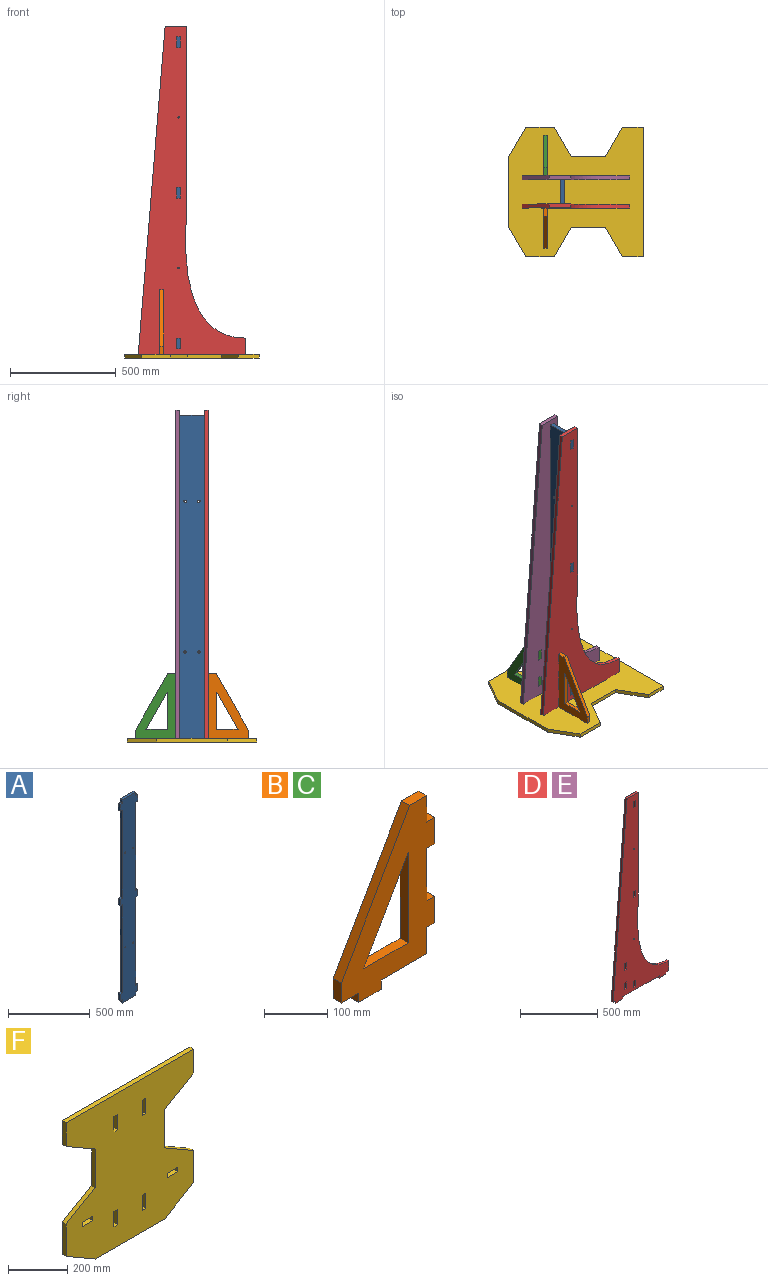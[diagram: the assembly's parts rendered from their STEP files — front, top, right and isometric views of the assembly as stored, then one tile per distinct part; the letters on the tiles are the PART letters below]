
ASSEMBLY  parts=6 mates=5
PART A: 34 faces, bbox 152.4x18x1524 mm
  f0: plane 25.4x18.03mm, normal (1,0,0), area 458.1mm2, adj f1,f30,f32,f33
  f1: plane 18.03x18.03mm, normal (0,0,-1), area 325.2mm2, adj f0,f2,f32,f33
  f2: plane 50.8x18.03mm, normal (1,0,0), area 916.1mm2, adj f1,f3,f32,f33
  f3: plane 18.03x18.03mm, normal (0,0,1), area 325.2mm2, adj f2,f4,f32,f33
  f4: plane 660.4x18.03mm, normal (1,0,0), area 11909.7mm2, adj f3,f5,f32,f33
  f5: plane 18.03x18.03mm, normal (0,0,-1), area 325.2mm2, adj f4,f6,f32,f33
  f6: plane 50.8x18.03mm, normal (1,0,0), area 916.1mm2, adj f5,f7,f32,f33
  f7: plane 18.03x18.03mm, normal (0,0,1), area 325.2mm2, adj f6,f8,f32,f33
  f8: plane 660.4x18.03mm, normal (1,0,0), area 11909.7mm2, adj f7,f9,f32,f33
  f9: plane 18.03x18.03mm, normal (0,0,-1), area 325.2mm2, adj f8,f10,f32,f33
  f10: plane 50.8x18.03mm, normal (1,0,0), area 916.1mm2, adj f9,f11,f32,f33
  f11: plane 18.03x18.03mm, normal (0,0,1), area 325.2mm2, adj f10,f12,f32,f33
  f12: plane 25.4x18.03mm, normal (1,0,0), area 458.1mm2, adj f11,f13,f32,f33
  f13: plane 116.33x18.03mm, normal (0,0,1), area 2097.9mm2, adj f12,f14,f32,f33
  f14: plane 25.4x18.03mm, normal (-1,0,0), area 458.1mm2, adj f13,f15,f32,f33
  f15: plane 18.03x18.03mm, normal (0,0,1), area 325.2mm2, adj f14,f16,f32,f33
  f16: plane 50.8x18.03mm, normal (-1,0,0), area 916.1mm2, adj f15,f17,f32,f33
  f17: plane 18.03x18.03mm, normal (0,0,-1), area 325.2mm2, adj f16,f18,f32,f33
  f18: plane 660.4x18.03mm, normal (-1,0,0), area 11909.7mm2, adj f17,f19,f32,f33
  f19: plane 18.03x18.03mm, normal (0,0,1), area 325.2mm2, adj f18,f20,f32,f33
  f20: plane 50.8x18.03mm, normal (-1,0,0), area 916.1mm2, adj f19,f21,f32,f33
  f21: plane 18.03x18.03mm, normal (0,0,-1), area 325.2mm2, adj f20,f22,f32,f33
  f22: plane 660.4x18.03mm, normal (-1,0,0), area 11909.7mm2, adj f21,f23,f32,f33
  f23: plane 18.03x18.03mm, normal (0,0,1), area 325.2mm2, adj f22,f24,f32,f33
  f24: plane 50.8x18.03mm, normal (-1,0,0), area 916.1mm2, adj f23,f25,f32,f33
  f25: plane 18.03x18.03mm, normal (0,0,-1), area 325.2mm2, adj f24,f26,f32,f33
  f26: plane 25.4x18.03mm, normal (-1,0,0), area 458.1mm2, adj f25,f30,f32,f33
  f27: cylinder r=5.59mm len=18.03mm, axis (0,1,0), area 633.2mm2, adj f32,f33
  f28: cylinder r=5.59mm len=18.03mm, axis (0,1,0), area 633.2mm2, adj f32,f33
  f29: cylinder r=5.59mm len=18.03mm, axis (0,1,0), area 633.2mm2, adj f32,f33
  f30: plane 116.33x18.03mm, normal (0,0,-1), area 2097.9mm2, adj f0,f26,f32,f33
  f31: cylinder r=5.59mm len=18.03mm, axis (0,1,0), area 633.2mm2, adj f32,f33
  f32: plane 1524x152.4mm, normal (0,-1,0), area 182394.3mm2, adj f0,f1,f2,f3,f4,f5,f6,f7
  f33: plane 1524x152.4mm, normal (0,1,0), area 182394.3mm2, adj f0,f1,f2,f3,f4,f5,f6,f7
PART B: 22 faces, bbox 208.5x18x322.8 mm
  f0: plane 50.8x18.03mm, normal (1,0,0), area 916.1mm2, adj f1,f19,f20,f21
  f1: plane 18.03x18.03mm, normal (0,0,-1), area 325.2mm2, adj f0,f2,f20,f21
  f2: plane 50.8x18.03mm, normal (1,0,0), area 916.1mm2, adj f1,f3,f20,f21
  f3: plane 18.03x18.03mm, normal (0,0,1), area 325.2mm2, adj f2,f4,f20,f21
  f4: plane 101.6x18.03mm, normal (1,0,0), area 1832.3mm2, adj f3,f5,f20,f21
  f5: plane 18.03x18.03mm, normal (0,0,-1), area 325.2mm2, adj f4,f6,f20,f21
  f6: plane 50.8x18.03mm, normal (1,0,0), area 916.1mm2, adj f5,f7,f20,f21
  f7: plane 18.03x18.03mm, normal (0,0,1), area 325.2mm2, adj f6,f8,f20,f21
  f8: plane 50.8x18.03mm, normal (1,0,0), area 916.1mm2, adj f7,f9,f20,f21
  f9: plane 38.1x18.03mm, normal (0,0,1), area 687.1mm2, adj f8,f10,f20,f21
  f10: plane 266.7x152.4mm, normal (-0.87,0,0.5), area 5539.5mm2, adj f9,f11,f20,f21
  f11: plane 38.1x18.03mm, normal (-1,0,0), area 687.1mm2, adj f10,f12,f20,f21
  f12: plane 38.1x18.03mm, normal (0,0,-1), area 687.1mm2, adj f11,f13,f20,f21
  f13: plane 18.03x18.03mm, normal (-1,0,0), area 325.2mm2, adj f12,f14,f20,f21
  f14: plane 50.8x18.03mm, normal (0,0,-1), area 916.1mm2, adj f13,f15,f20,f21
  f15: plane 18.03x18.03mm, normal (1,0,0), area 325.2mm2, adj f14,f19,f20,f21
  f16: plane 174.78x18.03mm, normal (-1,0,0), area 3151.9mm2, adj f17,f18,f20,f21
  f17: plane 99.87x18.03mm, normal (0,0,1), area 1801.1mm2, adj f16,f18,f20,f21
  f18: plane 174.78x99.87mm, normal (0.87,0,-0.5), area 3630.2mm2, adj f16,f17,f20,f21
  f19: plane 101.6x18.03mm, normal (0,0,-1), area 1832.3mm2, adj f0,f15,f20,f21
  f20: plane 322.83x208.53mm, normal (0,-1,0), area 31762.6mm2, adj f0,f1,f2,f3,f4,f5,f6,f7
  f21: plane 322.83x208.53mm, normal (0,1,0), area 31762.6mm2, adj f0,f1,f2,f3,f4,f5,f6,f7
PART C: same geometry as B
PART D: 38 faces, bbox 508x18x1567.4 mm
  f0: plane 25.4x18.03mm, normal (0,0,-1), area 458.1mm2, adj f1,f35,f36,f37
  f1: plane 18.03x18.03mm, normal (-1,0,0), area 325.2mm2, adj f0,f2,f36,f37
  f2: plane 63.5x18.03mm, normal (0,0,-1), area 1145.2mm2, adj f1,f3,f36,f37
  f3: plane 18.03x18.03mm, normal (1,0,0), area 325.2mm2, adj f2,f4,f36,f37
  f4: plane 330.2x18.03mm, normal (0,0,-1), area 5954.8mm2, adj f3,f5,f36,f37
  f5: plane 18.03x18.03mm, normal (-1,0,0), area 325.2mm2, adj f4,f6,f36,f37
  f6: plane 63.5x18.03mm, normal (0,0,-1), area 1145.2mm2, adj f5,f7,f36,f37
  f7: plane 18.03x18.03mm, normal (1,0,0), area 325.2mm2, adj f6,f8,f36,f37
  f8: plane 25.4x18.03mm, normal (0,0,-1), area 458.1mm2, adj f7,f9,f36,f37
  f9: plane 76.2x18.03mm, normal (1,0,0), area 1374.2mm2, adj f8,f10,f36,f37
  f10: extruded ~635x286.15mm, area 14161.2mm2, adj f9,f11,f36,f37
  f11: plane 838.2x18.03mm, normal (1,0,0), area 15116.1mm2, adj f10,f12,f36,f37
  f12: plane 101.6x18.03mm, normal (0,0,1), area 1832.3mm2, adj f11,f35,f36,f37
  f13: plane 50.8x18.03mm, normal (-1,0,0), area 916.1mm2, adj f14,f30,f36,f37
  f14: plane 18.03x18.03mm, normal (0,0,1), area 325.2mm2, adj f13,f15,f36,f37
  f15: plane 50.8x18.03mm, normal (1,0,0), area 916.1mm2, adj f14,f30,f36,f37
  f16: plane 50.8x18.03mm, normal (1,0,0), area 916.1mm2, adj f17,f31,f36,f37
  f17: plane 18.03x18.03mm, normal (0,0,-1), area 325.2mm2, adj f16,f18,f36,f37
  f18: plane 50.8x18.03mm, normal (-1,0,0), area 916.1mm2, adj f17,f31,f36,f37
  f19: plane 50.8x18.03mm, normal (1,0,0), area 916.1mm2, adj f20,f32,f36,f37
  f20: plane 18.03x18.03mm, normal (0,0,-1), area 325.2mm2, adj f19,f21,f36,f37
  f21: plane 50.8x18.03mm, normal (-1,0,0), area 916.1mm2, adj f20,f32,f36,f37
  f22: plane 18.03x18.03mm, normal (0,0,1), area 325.2mm2, adj f23,f33,f36,f37
  f23: plane 50.8x18.03mm, normal (1,0,0), area 916.1mm2, adj f22,f24,f36,f37
  f24: plane 18.03x18.03mm, normal (0,0,-1), area 325.2mm2, adj f23,f33,f36,f37
  f25: plane 50.8x18.03mm, normal (1,0,0), area 916.1mm2, adj f26,f34,f36,f37
  f26: plane 18.03x18.03mm, normal (0,0,-1), area 325.2mm2, adj f25,f27,f36,f37
  f27: plane 50.8x18.03mm, normal (-1,0,0), area 916.1mm2, adj f26,f34,f36,f37
  f28: cylinder r=3.3mm len=18.03mm, axis (0,1,0), area 374.2mm2, adj f36,f37
  f29: cylinder r=3.3mm len=18.03mm, axis (0,1,0), area 374.2mm2, adj f36,f37
  f30: plane 18.03x18.03mm, normal (0,0,-1), area 325.2mm2, adj f13,f15,f36,f37
  f31: plane 18.03x18.03mm, normal (0,0,1), area 325.2mm2, adj f16,f18,f36,f37
  f32: plane 18.03x18.03mm, normal (0,0,1), area 325.2mm2, adj f19,f21,f36,f37
  f33: plane 50.8x18.03mm, normal (-1,0,0), area 916.1mm2, adj f22,f24,f36,f37
  f34: plane 18.03x18.03mm, normal (0,0,1), area 325.2mm2, adj f25,f27,f36,f37
  f35: plane 1549.4x127mm, normal (-1,0,0.08), area 28035.6mm2, adj f0,f12,f36,f37
  f36: plane 1567.43x508mm, normal (0,-1,0), area 293554.6mm2, adj f0,f1,f2,f3,f4,f5,f6,f7
  f37: plane 1567.43x508mm, normal (0,1,0), area 293554.6mm2, adj f0,f1,f2,f3,f4,f5,f6,f7
PART E: same geometry as D
PART F: 40 faces, bbox 609.6x18x635 mm
  f0: plane 18.03x18.03mm, normal (0,0,-1), area 325.2mm2, adj f1,f37,f38,f39
  f1: plane 63.5x18.03mm, normal (-1,0,0), area 1145.2mm2, adj f0,f2,f38,f39
  f2: plane 18.03x18.03mm, normal (0,0,1), area 325.2mm2, adj f1,f37,f38,f39
  f3: plane 18.03x18.03mm, normal (0,0,-1), area 325.2mm2, adj f4,f31,f38,f39
  f4: plane 63.5x18.03mm, normal (-1,0,0), area 1145.2mm2, adj f3,f5,f38,f39
  f5: plane 18.03x18.03mm, normal (0,0,1), area 325.2mm2, adj f4,f31,f38,f39
  f6: plane 18.03x18.03mm, normal (0,0,-1), area 325.2mm2, adj f7,f32,f38,f39
  f7: plane 63.5x18.03mm, normal (-1,0,0), area 1145.2mm2, adj f6,f8,f38,f39
  f8: plane 18.03x18.03mm, normal (0,0,1), area 325.2mm2, adj f7,f32,f38,f39
  f9: plane 50.8x18.03mm, normal (0,0,1), area 916.1mm2, adj f10,f33,f38,f39
  f10: plane 18.03x18.03mm, normal (1,0,0), area 325.2mm2, adj f9,f11,f38,f39
  f11: plane 50.8x18.03mm, normal (0,0,-1), area 916.1mm2, adj f10,f33,f38,f39
  f12: plane 18.03x18.03mm, normal (-1,0,0), area 325.2mm2, adj f13,f34,f38,f39
  f13: plane 50.8x18.03mm, normal (0,0,1), area 916.1mm2, adj f12,f14,f38,f39
  f14: plane 18.03x18.03mm, normal (1,0,0), area 325.2mm2, adj f13,f34,f38,f39
  f15: plane 331.34x18.03mm, normal (0,0,-1), area 5975.3mm2, adj f16,f35,f38,f39
  f16: plane 139.13x80.33mm, normal (0.5,0,-0.87), area 2897.3mm2, adj f15,f17,f38,f39
  f17: plane 134.56x18.03mm, normal (1,0,0), area 2426.6mm2, adj f16,f18,f38,f39
  f18: plane 139.13x80.33mm, normal (0.5,0,0.87), area 2897.3mm2, adj f17,f19,f38,f39
  f19: plane 160.66x18.03mm, normal (1,0,0), area 2897.3mm2, adj f18,f20,f38,f39
  f20: plane 139.13x80.33mm, normal (0.5,0,-0.87), area 2897.3mm2, adj f19,f21,f38,f39
  f21: plane 98.81x18.03mm, normal (1,0,0), area 1781.9mm2, adj f20,f22,f38,f39
  f22: plane 609.6x18.03mm, normal (0,0,1), area 10993.5mm2, adj f21,f23,f38,f39
  f23: plane 98.81x18.03mm, normal (-1,0,0), area 1781.9mm2, adj f22,f24,f38,f39
  f24: plane 139.13x80.33mm, normal (-0.5,0,-0.87), area 2897.3mm2, adj f23,f25,f38,f39
  f25: plane 160.66x18.03mm, normal (-1,0,0), area 2897.3mm2, adj f24,f26,f38,f39
  f26: plane 139.13x80.33mm, normal (-0.5,0,0.87), area 2897.3mm2, adj f25,f27,f38,f39
  f27: plane 134.56x18.03mm, normal (-1,0,0), area 2426.6mm2, adj f26,f35,f38,f39
  f28: plane 63.5x18.03mm, normal (1,0,0), area 1145.2mm2, adj f29,f36,f38,f39
  f29: plane 18.03x18.03mm, normal (0,0,-1), area 325.2mm2, adj f28,f30,f38,f39
  f30: plane 63.5x18.03mm, normal (-1,0,0), area 1145.2mm2, adj f29,f36,f38,f39
  f31: plane 63.5x18.03mm, normal (1,0,0), area 1145.2mm2, adj f3,f5,f38,f39
  f32: plane 63.5x18.03mm, normal (1,0,0), area 1145.2mm2, adj f6,f8,f38,f39
  f33: plane 18.03x18.03mm, normal (-1,0,0), area 325.2mm2, adj f9,f11,f38,f39
  f34: plane 50.8x18.03mm, normal (0,0,-1), area 916.1mm2, adj f12,f14,f38,f39
  f35: plane 139.13x80.33mm, normal (-0.5,0,-0.87), area 2897.3mm2, adj f15,f27,f38,f39
  f36: plane 18.03x18.03mm, normal (0,0,1), area 325.2mm2, adj f28,f30,f38,f39
  f37: plane 63.5x18.03mm, normal (1,0,0), area 1145.2mm2, adj f0,f2,f38,f39
  f38: plane 635x609.6mm, normal (0,-1,0), area 302450.6mm2, adj f0,f1,f2,f3,f4,f5,f6,f7
  f39: plane 635x609.6mm, normal (0,1,0), area 302450.6mm2, adj f0,f1,f2,f3,f4,f5,f6,f7
PLACE A rot(axis=(0,0,-1),90deg) t=(-723.43,-44.02,-388.33)mm
PLACE B rot(axis=(0,0,1),90deg) t=(-821.35,-44.02,-58.13)mm
PLACE C rot(axis=(0,0,-1),90deg) t=(-803.31,-44.02,-58.13)mm
PLACE D t=(-1108.11,-102.19,-388.33)mm
PLACE E t=(-1108.11,32.18,-388.33)mm
PLACE F rot(axis=(-0.58,0.58,-0.58),120deg) t=(766.15,-44.02,-1168.36)mm fixed
MATE fastened D.f36 <-> B.f4  axis (0,-1,0) through (-812.33,-120.22,-947.13)mm
MATE fastened D.f8 <-> F.f38  axis (0,0,-1) through (-440.35,-111.2,-1150.33)mm
MATE fastened E.f37 <-> C.f8  axis (0,1,0) through (-812.33,32.18,-896.33)mm
MATE fastened A.f4 <-> D.f37  axis (0,-1,0) through (-732.45,-102.19,-1074.13)mm
MATE fastened E.f36 <-> A.f26  axis (0,-1,0) through (-732.45,14.15,-1124.93)mm
